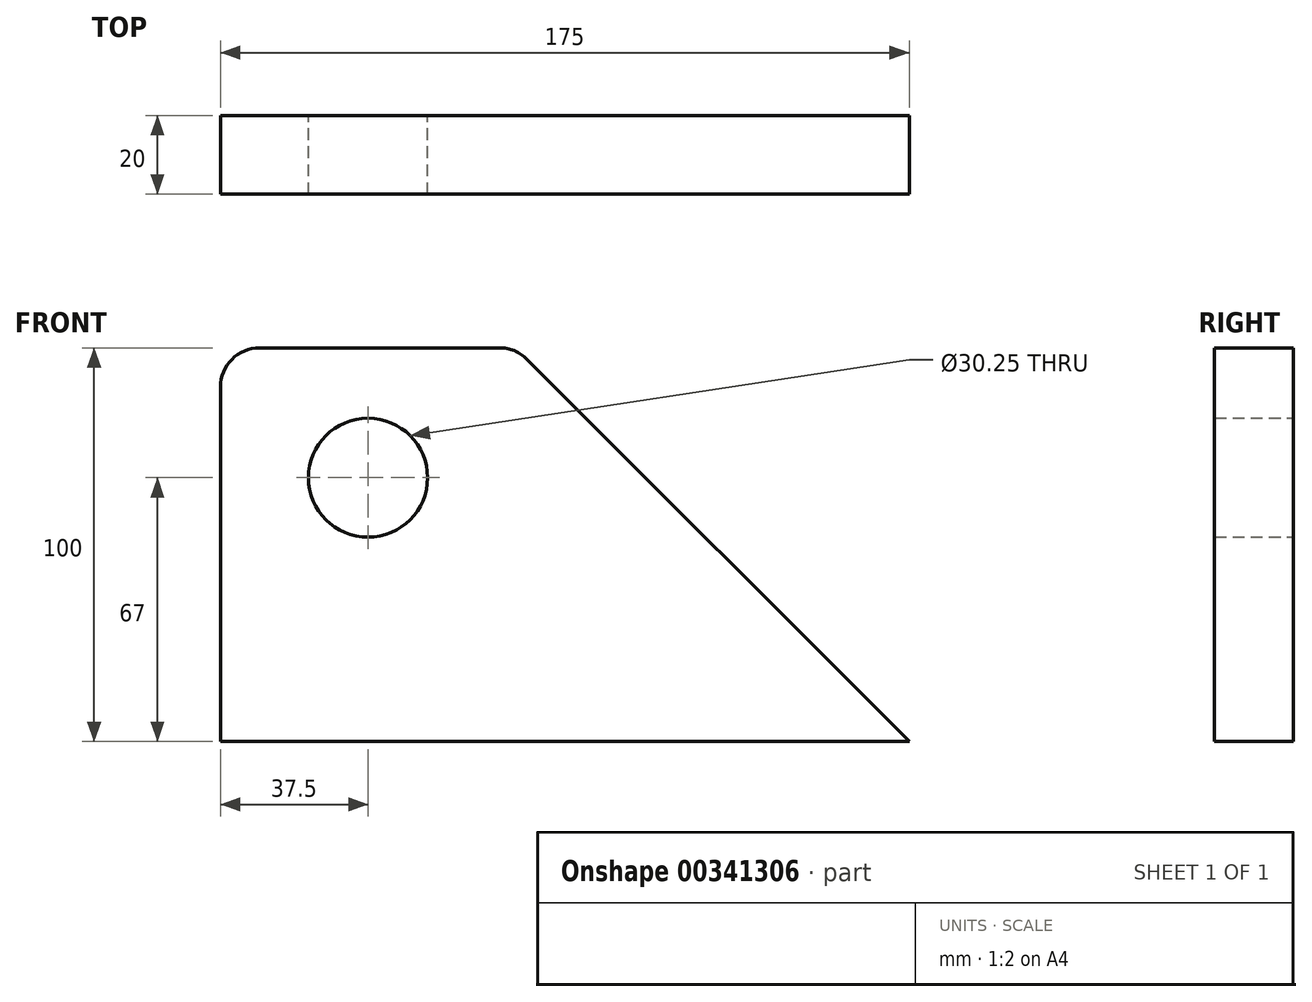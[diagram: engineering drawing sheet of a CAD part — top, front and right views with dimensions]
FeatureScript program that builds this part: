
annotation { "Feature Type Name" : "Feature", "Feature Type Description" : "" }
export const myFeature = defineFeature(function(context is Context, id is Id, definition is map)
    precondition{}
    {
        {
            var Q0;
            Q0=qCreatedBy(makeId("Front.planeOp"),FACE);
            var sketch = newSketch(context, id + "F0", { "sketchPlane" : qUnion([Q0])});
            skLineSegment(sketch, "E0.bottom", {"start": v(0, 0) * mm, "end": v(150, 0) * mm});
            skLineSegment(sketch, "E0.top", {"start": v(0, 100) * mm, "end": v(75, 100) * mm});
            skLineSegment(sketch, "E0.left", {"start": v(0, 0) * mm, "end": v(0, 100) * mm});
            skPoint(sketch, "E1", {"position": v(37.5, 67) * mm});
            skCircle(sketch, "E2", {"center": v(37.5, 67) * mm, "radius": 15.12 * mm});
            skLineSegment(sketch, "E3", {"start": v(75, 100) * mm, "end": v(175, 0) * mm});
            skLineSegment(sketch, "E4", {"start": v(0, 0) * mm, "end": v(175, 0) * mm});
            skPoint(sketch, "E5.orphan", {"position": v(150, 100) * mm});
            skSolve(sketch);
        }
        {
            var Q0;
            Q0=makeQuery(id+"F0.imprint","IMPRINT",FACE,{"disambiguationData":[TD([[makeQuery(id+"F0.imprint","IMPRINT",EDGE,{"derivedFrom":sQuery(id+"F0.wireOp",EDGE,"E0.bottom")}),1.0]])]});
            var Q1;
            Q1=makeQuery(id+"F0.imprint","IMPRINT",FACE,{"disambiguationData":[TD([[makeQuery(id+"F0.imprint","IMPRINT",EDGE,{"derivedFrom":sQuery(id+"F0.wireOp",EDGE,"E0.top")}),-1.0]])]});
            extrude(context, id + "F1", {"entities" : qUnion([Q0, Q1]), "depth" : 20 * mm});
        }
        {
            var Q0;
            Q0=makeQuery(id+"F1.opExtrude","SWEPT_EDGE",EDGE,{"disambiguationData":[OSD([sQuery(id+"F0.wireOp",EDGE,"E0.top"),sQuery(id+"F0.wireOp",EDGE,"E0.left")])]});
            fillet(context, id + "F2", {"entities" : qUnion([Q0]), "radius" : 10 * mm, "tangentPropagation" : true, "allowEdgeOverflow" : false});
        }
        {
            var Q0;
            Q0=makeQuery(id+"F1.opExtrude","SWEPT_EDGE",EDGE,{"disambiguationData":[OSD([sQuery(id+"F0.wireOp",EDGE,"E0.top"),sQuery(id+"F0.wireOp",EDGE,"E3")])]});
            fillet(context, id + "F3", {"entities" : qUnion([Q0]), "radius" : 10 * mm, "tangentPropagation" : true, "allowEdgeOverflow" : false});
        }
    });
